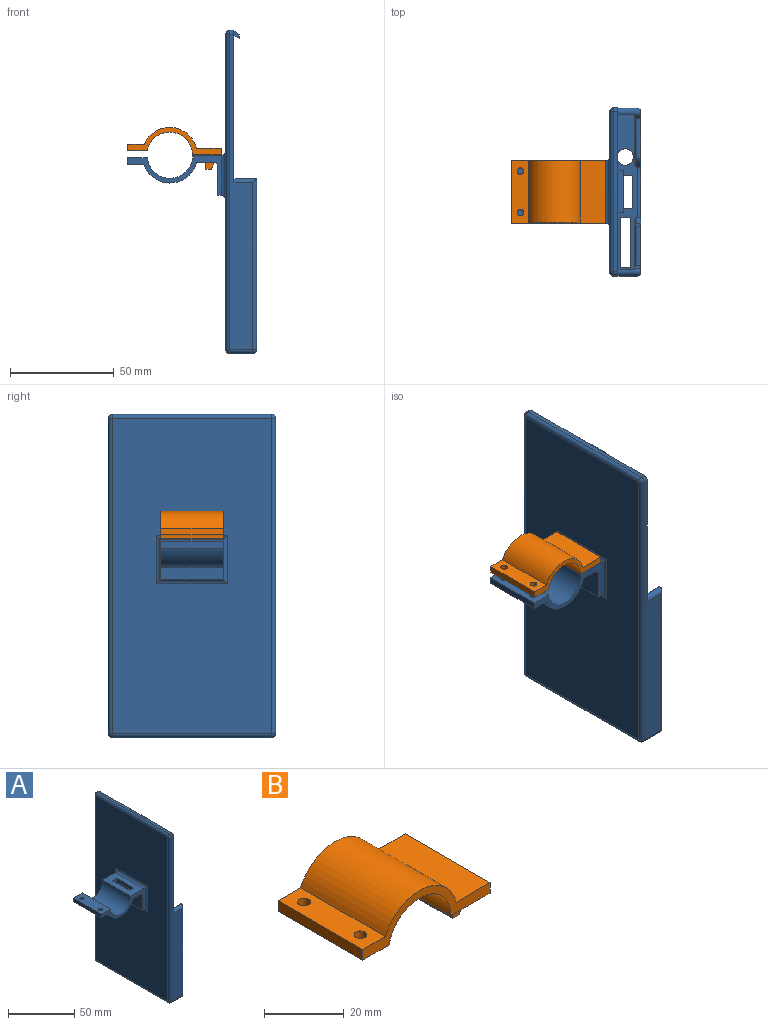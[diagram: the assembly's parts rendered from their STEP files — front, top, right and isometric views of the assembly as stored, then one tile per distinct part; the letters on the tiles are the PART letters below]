
ASSEMBLY  parts=2 mates=1
PART A: 93 faces, bbox 62.5x81x156 mm
  f0: plane 82.51x25.31mm, normal (1,0,0), area 245.7mm2, adj f57,f61,f66,f89,f90,f91
  f1: plane 21.5x11mm, normal (0,0,-1), area 189mm2, adj f59,f65,f66,f75
  f2: plane 55.5x11mm, normal (0,0,-1), area 153mm2, adj f59,f60,f66,f75,f76,f77,f78,f79
  f3: plane 75x9.5mm, normal (0,0,1), area 353.8mm2, adj f4,f29,f30,f32,f34,f40,f41,f42
  f4: plane 154.5x81mm, normal (1,0,0), area 11876.5mm2, adj f3,f24,f25,f26,f29,f30,f36,f38
  f5: cylinder r=11mm len=30mm, axis (0,1,0), area 1006.7mm2, adj f6,f11,f12,f13
  f6: plane 30x9.65mm, normal (0,0,1), area 273.3mm2, adj f5,f7,f12,f13,f14,f16
  f7: plane 30x3.25mm, normal (-1,0,0), area 97.5mm2, adj f6,f8,f12,f13
  f8: plane 30x8mm, normal (0,0,-1), area 240mm2, adj f7,f9,f12,f13
  f9: cylinder r=13.3mm len=30mm, axis (0,1,0), area 1025mm2, adj f8,f10,f12,f13
  f10: plane 30x8.11mm, normal (0,0,-1), area 162.2mm2, adj f9,f12,f13,f18,f19,f20,f21,f70
  f11: plane 30x13.89mm, normal (0,0,1), area 335.8mm2, adj f5,f12,f13,f18,f19,f20,f21,f71
  f12: plane 45.49x19.25mm, normal (0,-1,0), area 179.4mm2, adj f5,f6,f7,f8,f9,f10,f11,f22
  f13: plane 45.49x19.25mm, normal (0,1,0), area 179.4mm2, adj f5,f6,f7,f8,f9,f10,f11,f22
  f14: cylinder r=1.6mm len=3.2mm, axis (0,0,-1), area 22.6mm2, adj f6,f15
  f15: plane 3.2x3.2mm, normal (0,0,1), area 8mm2, adj f14
  f16: cylinder r=1.6mm len=3.2mm, axis (0,0,-1), area 22.6mm2, adj f6,f17
  f17: plane 3.2x3.2mm, normal (0,0,1), area 8mm2, adj f16
  f18: plane 18x3.25mm, normal (-1,0,0), area 58.5mm2, adj f10,f11,f19,f21
  f19: plane 4.5x3.25mm, normal (0,-1,0), area 14.6mm2, adj f10,f11,f18,f20
  f20: plane 18x3.25mm, normal (1,0,0), area 58.5mm2, adj f10,f11,f19,f21
  f21: plane 4.5x3.25mm, normal (0,1,0), area 14.6mm2, adj f10,f11,f18,f20
  f22: plane 30x14mm, normal (-1,0,0), area 420mm2, adj f12,f13,f23,f70
  f23: plane 30x1.89mm, normal (0,0,-1), area 56.8mm2, adj f12,f13,f22,f74
  f24: plane 152x11mm, normal (0,-1,0), area 1028.5mm2, adj f4,f49,f53,f57,f60,f61
  f25: plane 152x11mm, normal (0,1,0), area 1028.5mm2, adj f4,f51,f58,f65,f67,f69
  f26: plane 77x2mm, normal (0,0,1), area 154mm2, adj f4,f35,f49,f51,f52
  f27: plane 152x77mm, normal (-1,0,0), area 10913.5mm2, adj f52,f53,f58,f59,f71,f72,f73,f74
  f28: plane 3x1.75mm, normal (0,-0.77,0.64), area 5.3mm2, adj f67,f84
  f29: plane 80.7x8mm, normal (0,-1,0), area 645.6mm2, adj f3,f4,f32,f64
  f30: plane 80.7x8mm, normal (0,1,0), area 645.6mm2, adj f3,f4,f34,f54
  f31: plane 3x1.75mm, normal (0,0.77,0.64), area 5.3mm2, adj f57,f89
  f32: plane 81.29x23.82mm, normal (-1,0,0), area 139.2mm2, adj f3,f29,f64,f67,f84,f85,f87
  f33: plane 82.51x25.31mm, normal (1,0,0), area 245.7mm2, adj f66,f67,f69,f84,f85,f87
  f34: plane 81.29x23.82mm, normal (-1,0,0), area 139.2mm2, adj f3,f30,f54,f57,f89,f90,f91
  f35: plane 20x2.5mm, normal (0.67,0,0.74), area 67.3mm2, adj f26,f37,f38,f39
  f36: plane 20x2.5mm, normal (-0.42,0,-0.91), area 55.2mm2, adj f4,f37,f38,f39
  f37: plane 20x1.5mm, normal (1,0,0), area 30mm2, adj f35,f36,f38,f39
  f38: plane 3.75x2.5mm, normal (0,1,0), area 5.1mm2, adj f4,f35,f36,f37
  f39: plane 3.75x2.5mm, normal (0,-1,0), area 5.1mm2, adj f4,f35,f36,f37
  f40: plane 7x1.5mm, normal (0,1,0), area 10.5mm2, adj f3,f4,f42,f76
  f41: plane 7x1.5mm, normal (0,-1,0), area 10.5mm2, adj f3,f4,f42,f79
  f42: plane 16x1.5mm, normal (-1,0,0), area 24mm2, adj f3,f40,f41,f78
  f43: plane 24.5x1.5mm, normal (1,0,0), area 36.8mm2, adj f3,f44,f45,f83
  f44: plane 5x1.5mm, normal (0,1,0), area 7.5mm2, adj f3,f43,f46,f82
  f45: plane 5x1.5mm, normal (0,-1,0), area 7.5mm2, adj f3,f43,f46,f81
  f46: plane 24.5x1.5mm, normal (-1,0,0), area 36.8mm2, adj f3,f44,f45,f80
  f47: plane 3.87x0.5mm, normal (0,0,-1), area 1.3mm2, adj f4,f48
  f48: cylinder r=4mm len=8mm, axis (0,0,-1), area 37.7mm2, adj f3,f47,f75
  f49: cylinder r=2mm len=2mm, axis (1,0,0), area 6.3mm2, adj f4,f24,f26,f50
  f50: sphere r=2mm, area 6.3mm2, adj f49,f52,f53
  f51: cylinder r=2mm len=2mm, axis (-1,0,0), area 6.3mm2, adj f4,f25,f26,f55
  f52: cylinder r=2mm len=77mm, axis (0,-1,0), area 241.9mm2, adj f26,f27,f50,f55
  f53: cylinder r=2mm len=152mm, axis (0,0,-1), area 477.5mm2, adj f24,f27,f50,f56
  f54: cylinder r=2mm len=8mm, axis (-1,0,0), area 4.8mm2, adj f4,f30,f34,f57
  f55: sphere r=2mm, area 6.3mm2, adj f51,f52,f58
  f56: sphere r=2mm, area 6.3mm2, adj f53,f59,f60
  f57: cylinder r=2mm len=11mm, axis (1,0,0), area 45.1mm2, adj f0,f4,f24,f31,f34,f54,f61,f89
  f58: cylinder r=2mm len=152mm, axis (0,0,1), area 477.5mm2, adj f25,f27,f55,f62
  f59: cylinder r=2mm len=77mm, axis (0,1,0), area 241.9mm2, adj f1,f2,f27,f56,f62
  f60: cylinder r=2mm len=11mm, axis (-1,0,0), area 34.6mm2, adj f2,f24,f56,f63
  f61: cylinder r=2mm len=82.51mm, axis (0,0,1), area 256.9mm2, adj f0,f24,f57,f63
  f62: sphere r=2mm, area 6.3mm2, adj f58,f59,f65
  f63: sphere r=2mm, area 6.3mm2, adj f60,f61,f66
  f64: cylinder r=2mm len=8mm, axis (-1,0,0), area 4.8mm2, adj f4,f29,f32,f67
  f65: cylinder r=2mm len=11mm, axis (1,0,0), area 34.6mm2, adj f1,f25,f62,f68
  f66: cylinder r=2mm len=77mm, axis (0,-1,0), area 234.9mm2, adj f0,f1,f2,f33,f63,f68,f87,f88
  f67: cylinder r=2mm len=11mm, axis (-1,0,0), area 45.1mm2, adj f4,f25,f28,f32,f33,f64,f69,f84
  f68: sphere r=2mm, area 6.3mm2, adj f65,f66,f69
  f69: cylinder r=2mm len=82.51mm, axis (0,0,-1), area 256.9mm2, adj f25,f33,f67,f68
  f70: cylinder r=2mm len=30mm, axis (0,1,0), area 94.2mm2, adj f10,f12,f13,f22
  f71: cylinder r=2mm len=34mm, axis (0,1,0), area 98.8mm2, adj f11,f27,f72,f73
  f72: cylinder r=2mm len=23.25mm, axis (0,0,-1), area 65mm2, adj f12,f27,f71,f74
  f73: cylinder r=2mm len=23.25mm, axis (0,0,1), area 65mm2, adj f13,f27,f71,f74
  f74: cylinder r=2mm len=34mm, axis (0,1,0), area 98.8mm2, adj f23,f27,f72,f73
  f75: torus R=5.5mm, axis (0,0,1), area 67.3mm2, adj f1,f2,f48
  f76: cylinder r=1.5mm len=10mm, axis (-1,0,0), area 19.1mm2, adj f2,f40,f77,f78
  f77: cylinder r=1.5mm len=19mm, axis (0,1,0), area 40.3mm2, adj f2,f4,f76,f79
  f78: cylinder r=1.5mm len=19mm, axis (0,-1,0), area 40.3mm2, adj f2,f42,f76,f79
  f79: cylinder r=1.5mm len=10mm, axis (1,0,0), area 19.1mm2, adj f2,f41,f77,f78
  f80: cylinder r=1.5mm len=27.5mm, axis (0,-1,0), area 60.3mm2, adj f2,f46,f81,f82
  f81: cylinder r=1.5mm len=8mm, axis (1,0,0), area 14.3mm2, adj f2,f45,f80,f83
  f82: cylinder r=1.5mm len=8mm, axis (-1,0,0), area 14.3mm2, adj f2,f44,f80,f83
  f83: cylinder r=1.5mm len=27.5mm, axis (0,1,0), area 60.3mm2, adj f2,f43,f81,f82
  f84: cylinder r=1.5mm len=76.33mm, axis (0,0,-1), area 349.8mm2, adj f28,f32,f33,f67,f85
  f85: cylinder r=1.5mm len=20.63mm, axis (0,-1,0), area 92.7mm2, adj f32,f33,f84,f86
  f86: sphere r=1.5mm, area 4.7mm2, adj f85,f87
  f87: cylinder r=1.5mm len=6.63mm, axis (0,-0.5,-0.87), area 28.5mm2, adj f3,f32,f33,f66,f86,f88
  f88: cylinder r=1.5mm len=25.54mm, axis (0,1,0), area 52.2mm2, adj f3,f66,f87,f90
  f89: cylinder r=1.5mm len=76.33mm, axis (0,0,-1), area 349.8mm2, adj f0,f31,f34,f57,f91
  f90: cylinder r=1.5mm len=6.63mm, axis (0,0.5,-0.87), area 28.5mm2, adj f0,f3,f34,f66,f88,f92
  f91: cylinder r=1.5mm len=20.63mm, axis (0,1,0), area 92.7mm2, adj f0,f34,f89,f92
  f92: sphere r=1.5mm, area 4.7mm2, adj f90,f91
PART B: 19 faces, bbox 45.1x30x20.3 mm
  f0: plane 18x3.75mm, normal (1,0,0), area 67.5mm2, adj f1,f13,f15,f18
  f1: plane 30x13.89mm, normal (0,0,-1), area 371.8mm2, adj f0,f2,f3,f9,f10,f13,f14,f15
  f2: cylinder r=11mm len=30mm, axis (0,1,0), area 976.4mm2, adj f1,f8,f9,f10
  f3: plane 30x3.25mm, normal (1,0,0), area 97.5mm2, adj f1,f4,f9,f10
  f4: plane 30x12mm, normal (0,0,1), area 360mm2, adj f3,f5,f9,f10
  f5: cylinder r=13.3mm len=30mm, axis (0,1,0), area 992.9mm2, adj f4,f6,f9,f10
  f6: plane 30x8mm, normal (0,0,1), area 223.9mm2, adj f5,f7,f9,f10,f11,f12
  f7: plane 30x3.25mm, normal (-1,0,0), area 97.5mm2, adj f6,f8,f9,f10
  f8: plane 30x9.4mm, normal (0,0,-1), area 265.9mm2, adj f2,f7,f9,f10,f11,f12
  f9: plane 45.11x13.3mm, normal (0,-1,0), area 145.5mm2, adj f1,f2,f3,f4,f5,f6,f7,f8
  f10: plane 45.11x13.3mm, normal (0,1,0), area 145.5mm2, adj f1,f2,f3,f4,f5,f6,f7,f8
  f11: cylinder r=1.6mm len=3.25mm, axis (0,0,1), area 32.7mm2, adj f6,f8
  f12: cylinder r=1.6mm len=3.25mm, axis (0,0,1), area 32.7mm2, adj f6,f8
  f13: plane 7x4mm, normal (0,-1,0), area 19.9mm2, adj f0,f1,f14,f16,f17,f18
  f14: plane 18x7mm, normal (-1,0,0), area 126mm2, adj f1,f13,f15,f16
  f15: plane 7x4mm, normal (0,1,0), area 19.9mm2, adj f0,f1,f14,f16,f17,f18
  f16: plane 18x2.5mm, normal (0,0,-1), area 45mm2, adj f13,f14,f15,f17
  f17: plane 18x3.25mm, normal (0.91,0,-0.42), area 64.4mm2, adj f13,f15,f16,f18
  f18: plane 18x1.5mm, normal (0,0,1), area 27mm2, adj f0,f13,f15,f17
PLACE A t=(-3.12,0.07,20.9)mm fixed
PLACE B t=(-3.25,0.07,1.15)mm
MATE slider B.f7 <-> A.f7  axis (-1,0,0) through (-23.47,0.07,4.78)mm
